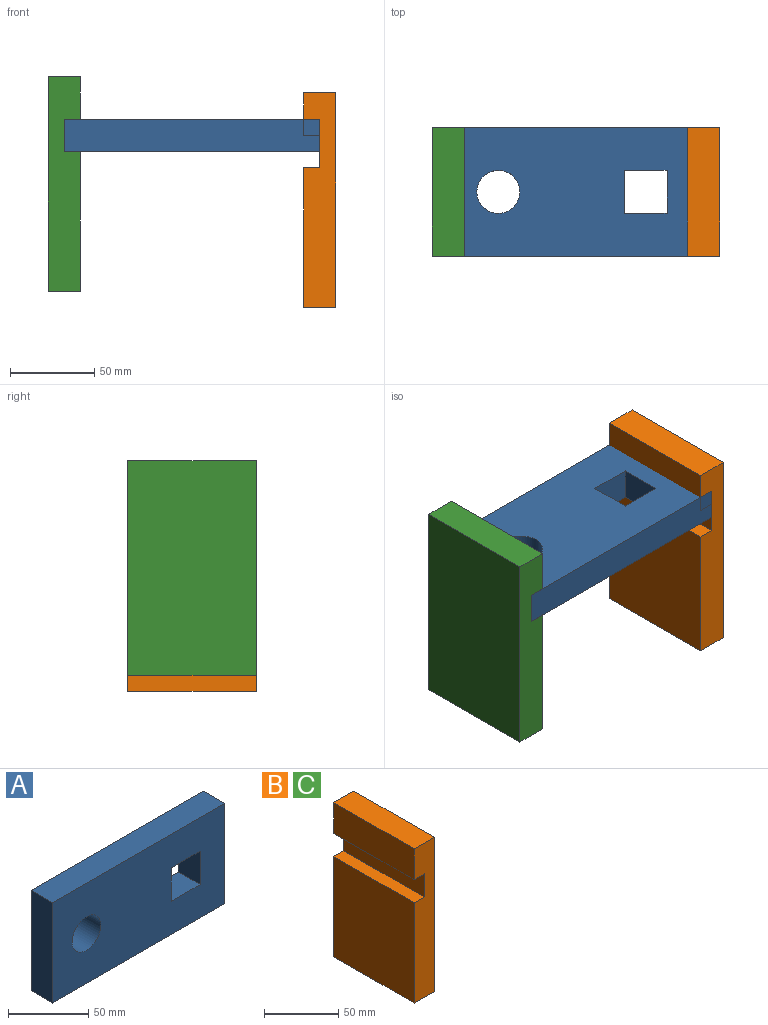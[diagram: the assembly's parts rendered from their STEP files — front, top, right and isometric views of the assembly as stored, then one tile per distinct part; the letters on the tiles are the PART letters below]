
ASSEMBLY  parts=3 mates=2
PART A: 11 faces, bbox 151.1x19.1x76.2 mm
  f0: plane 76.2x19.05mm, normal (-1,0,0), area 1451.6mm2, adj f1,f3,f4,f5
  f1: plane 151.13x19.05mm, normal (0,0,-1), area 2879mm2, adj f0,f2,f4,f5
  f2: plane 76.2x19.05mm, normal (1,0,0), area 1451.6mm2, adj f1,f3,f4,f5
  f3: plane 151.13x19.05mm, normal (0,0,1), area 2879mm2, adj f0,f2,f4,f5
  f4: plane 151.13x76.2mm, normal (0,-1,0), area 10364.2mm2, adj f0,f1,f2,f3,f6,f7,f8,f9
  f5: plane 151.13x76.2mm, normal (0,1,0), area 10364.2mm2, adj f0,f1,f2,f3,f6,f7,f8,f9
  f6: plane 25.4x19.05mm, normal (1,0,0), area 483.9mm2, adj f4,f5,f7,f9
  f7: plane 25.4x19.05mm, normal (0,0,1), area 483.9mm2, adj f4,f5,f6,f8
  f8: plane 25.4x19.05mm, normal (-1,0,0), area 483.9mm2, adj f4,f5,f7,f9
  f9: plane 25.4x19.05mm, normal (0,0,-1), area 483.9mm2, adj f4,f5,f6,f8
  f10: cylinder r=12.7mm len=25.4mm, axis (0,-1,0), area 1520.1mm2, adj f4,f5
PART B: 10 faces, bbox 19.1x76.2x127 mm
  f0: plane 82.55x76.2mm, normal (-1,0,0), area 6290.3mm2, adj f1,f7,f8,f9
  f1: plane 76.2x19.05mm, normal (0,0,-1), area 1451.6mm2, adj f0,f2,f8,f9
  f2: plane 127x76.2mm, normal (1,0,0), area 9677.4mm2, adj f1,f3,f8,f9
  f3: plane 76.2x19.05mm, normal (0,0,1), area 1451.6mm2, adj f2,f4,f8,f9
  f4: plane 76.2x25.4mm, normal (-1,0,0), area 1935.5mm2, adj f3,f5,f8,f9
  f5: plane 76.2x9.53mm, normal (0,0,-1), area 725.8mm2, adj f4,f6,f8,f9
  f6: plane 76.2x19.05mm, normal (-1,0,0), area 1451.6mm2, adj f5,f7,f8,f9
  f7: plane 76.2x9.53mm, normal (0,0,1), area 725.8mm2, adj f0,f6,f8,f9
  f8: plane 127x19.05mm, normal (0,-1,0), area 2237.9mm2, adj f0,f1,f2,f3,f4,f5,f6,f7
  f9: plane 127x19.05mm, normal (0,1,0), area 2237.9mm2, adj f0,f1,f2,f3,f4,f5,f6,f7
PART C: same geometry as B
PLACE A rot(axis=(1,0,0),90deg) t=(-0.59,-5.07,10.47)mm
PLACE B t=(50.86,4.96,-35.89)mm
PLACE C rot(axis=(0,0,1),180deg) t=(-51.34,-71.24,-26.37)mm
MATE slider C.f6 <-> A.f0  axis (1,0,0) through (-75.81,-33.14,0.94)mm
MATE slider B.f6 <-> A.f2  axis (-1,0,0) through (75.32,-33.14,0.94)mm
